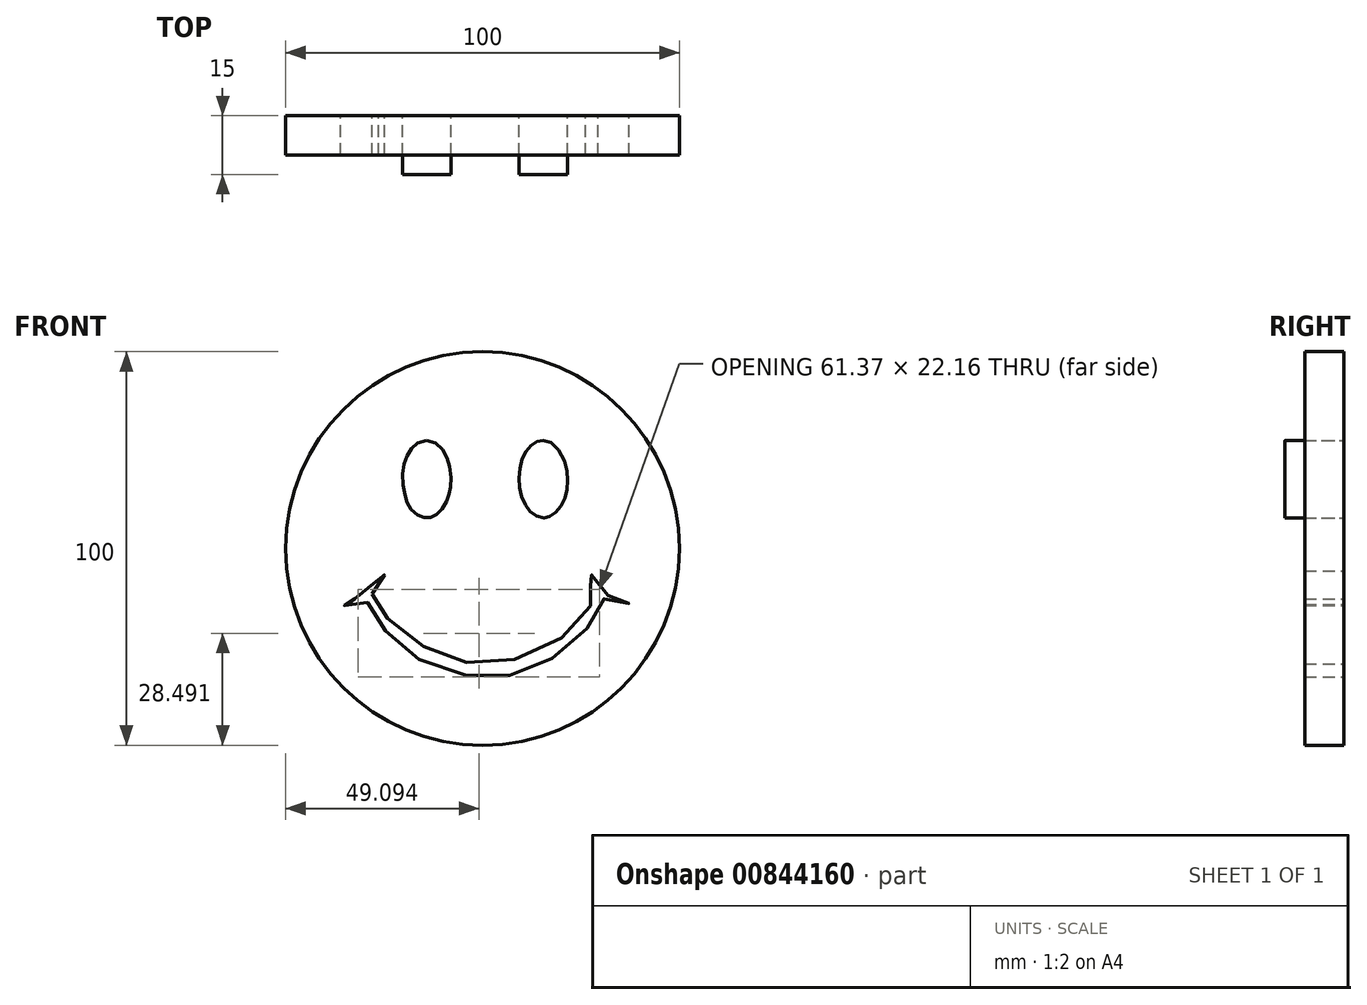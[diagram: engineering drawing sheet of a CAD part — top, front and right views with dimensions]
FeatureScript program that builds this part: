
annotation { "Feature Type Name" : "Feature", "Feature Type Description" : "" }
export const myFeature = defineFeature(function(context is Context, id is Id, definition is map)
    precondition{}
    {
        {
            var Q0;
            Q0=qCreatedBy(makeId("Front.planeOp"),FACE);
            var sketch = newSketch(context, id + "F0", { "sketchPlane" : qUnion([Q0])});
            skCircle(sketch, "E0", {"center": v(0, 0) * mm, "radius": 50 * mm});
            skSolve(sketch);
        }
        {
            var Q0;
            Q0=makeQuery(id+"F0.imprint","IMPRINT",FACE,{"disambiguationData":[TD([[makeQuery(id+"F0.imprint","IMPRINT",EDGE,{"derivedFrom":sQuery(id+"F0.wireOp",EDGE,"E0")}),1.0]])]});
            var sketch = newSketch(context, id + "F1", { "sketchPlane" : qUnion([Q0])});
            skFitSpline(sketch, "E1", {"points": [v(15.4, 27.46) * mm, v(18.08, 26.46) * mm, v(21.06, 21.63) * mm, v(21.63, 17.75) * mm, v(21.34, 14.48) * mm, v(20.3, 11.51) * mm, v(18.46, 9.03) * mm, v(16.8, 8.1) * mm, v(15.4, 7.73) * mm, v(13.03, 8.6) * mm, v(11.4, 10.32) * mm, v(9.8, 13.44) * mm, v(9.32, 16.75) * mm, v(9.51, 20.6) * mm, v(10.6, 23.93) * mm, v(12.18, 26.06) * mm, v(13.94, 27.23) * mm, v(15.4, 27.46) * mm]});
            skFitSpline(sketch, "E2", {"points": [v(-14.2, 27.45) * mm, v(-11.12, 26.19) * mm, v(-9.23, 23.48) * mm, v(-8.27, 20.32) * mm, v(-8.08, 16.03) * mm, v(-8.49, 14) * mm, v(-9.26, 11.8) * mm, v(-10.78, 9.53) * mm, v(-12.44, 8.2) * mm, v(-13.89, 7.83) * mm, v(-15.47, 8.03) * mm, v(-17.49, 9.2) * mm, v(-18.96, 11.4) * mm, v(-19.7, 13.55) * mm, v(-20.34, 17.65) * mm, v(-19.86, 21.58) * mm, v(-18.8, 24.27) * mm, v(-17.13, 26.42) * mm, v(-14.2, 27.45) * mm]});
            skSolve(sketch);
        }
        {
            var Q0;
            Q0 = qSketchRegion(id + "F1", true);
            extrude(context, id + "F2", {"entities" : qUnion([Q0]), "depth" : 15 * mm, "offsetDistance" : 25 * mm});
        }
        {
            var Q0;
            Q0 = qSketchRegion(id + "F0", true);
            extrude(context, id + "F3", {"entities" : qUnion([Q0]), "depth" : 10 * mm, "offsetDistance" : 25 * mm});
        }
        {
            var Q0;
            Q0=makeQuery(id+"F3.opExtrude","CAP_FACE",FACE,{"disambiguationData":[OSD([sQuery(id+"F0.wireOp",EDGE,"E0")])],"isStart":false});
            var sketch = newSketch(context, id + "F4", { "sketchPlane" : qUnion([Q0])});
            skFitSpline(sketch, "E3", {"points": [v(-28.12, -11.52) * mm, v(-26.74, -10.2) * mm, v(-25.66, -8.4) * mm, v(-24.88, -6.47) * mm, v(-25.06, -5.81) * mm, v(-26.08, -5.81) * mm, v(-26.32, -7.01) * mm, v(-27.82, -9.42) * mm, v(-29.8, -11.4) * mm, v(-32.57, -12.78) * mm, v(-35.64, -13.2) * mm, v(-36.12, -13.75) * mm, v(-35.7, -14.35) * mm, v(-33.77, -14.29) * mm, v(-29.69, -12.84) * mm, v(-29.63, -12.96) * mm, v(-28.85, -14.23) * mm, v(-27.04, -17.53) * mm, v(-23.86, -21.98) * mm, v(-18.87, -26.55) * mm, v(-8.17, -31.54) * mm, v(-1.86, -32.44) * mm, v(5.66, -32.44) * mm, v(13.05, -30.4) * mm, v(20.68, -25.83) * mm, v(26.4, -20.42) * mm, v(29.52, -15.49) * mm, v(30.84, -12.78) * mm, v(31.44, -13.08) * mm, v(34.93, -14.1) * mm, v(37.21, -13.93) * mm, v(36.8, -13.2) * mm, v(34.57, -12.78) * mm, v(31.56, -11.76) * mm, v(29.4, -10.02) * mm, v(28.02, -7.61) * mm, v(27.06, -5.75) * mm, v(26.21, -6.11) * mm, v(26.82, -8.16) * mm, v(28.44, -10.8) * mm, v(29.34, -11.7) * mm, v(27.84, -13.99) * mm, v(25.25, -17.83) * mm, v(17.62, -24.32) * mm, v(8.18, -28.17) * mm, v(-0.96, -29.25) * mm, v(-9, -27.51) * mm, v(-16.16, -24.26) * mm, v(-22, -20) * mm, v(-26.44, -14.83) * mm, v(-26.38, -14.53) * mm, v(-28.12, -11.52) * mm]});
            skSolve(sketch);
        }
        {
            var Q0;
            Q0 = qSketchRegion(id + "F4", true);
            extrude(context, id + "F5", {"entities" : qUnion([Q0]), "operationType" : NewBodyOperationType.REMOVE, "endBound" : BoundingType.SYMMETRIC, "oppositeDirection" : true, "depth" : 181.8 * mm, "offsetDistance" : 25 * mm});
        }
    });
